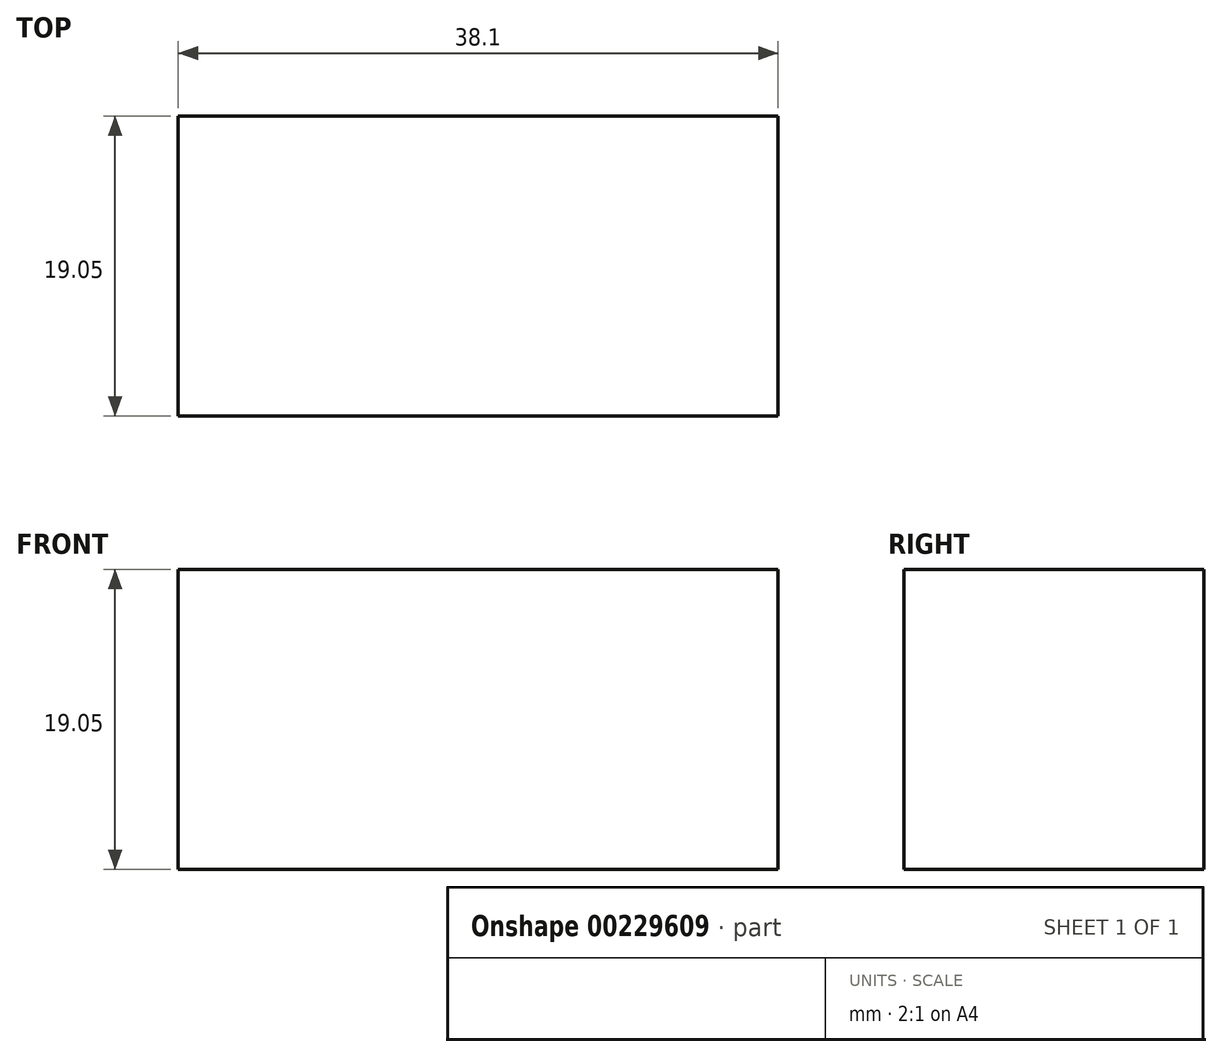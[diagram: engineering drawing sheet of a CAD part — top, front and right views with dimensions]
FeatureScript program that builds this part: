
annotation { "Feature Type Name" : "Feature", "Feature Type Description" : "" }
export const myFeature = defineFeature(function(context is Context, id is Id, definition is map)
    precondition{}
    {
        {
            var Q0;
            Q0=qCreatedBy(makeId("Top.planeOp"),FACE);
            var sketch = newSketch(context, id + "F0", { "sketchPlane" : qUnion([Q0])});
            skLineSegment(sketch, "E0.bottom", {"start": v(-17.22, 40.3) * mm, "end": v(20.88, 40.3) * mm});
            skLineSegment(sketch, "E0.top", {"start": v(-17.22, 21.25) * mm, "end": v(20.88, 21.25) * mm});
            skLineSegment(sketch, "E0.left", {"start": v(-17.22, 40.3) * mm, "end": v(-17.22, 21.25) * mm});
            skLineSegment(sketch, "E0.right", {"start": v(20.88, 40.3) * mm, "end": v(20.88, 21.25) * mm});
            skSolve(sketch);
        }
        {
            var Q0;
            Q0=makeQuery(id+"F0.imprint","IMPRINT",FACE,{"disambiguationData":[TD([[makeQuery(id+"F0.imprint","IMPRINT",EDGE,{"derivedFrom":sQuery(id+"F0.wireOp",EDGE,"E0.bottom")}),-1.0]])]});
            extrude(context, id + "F1", {"entities" : qUnion([Q0]), "depth" : 19.05 * mm});
        }
    });
